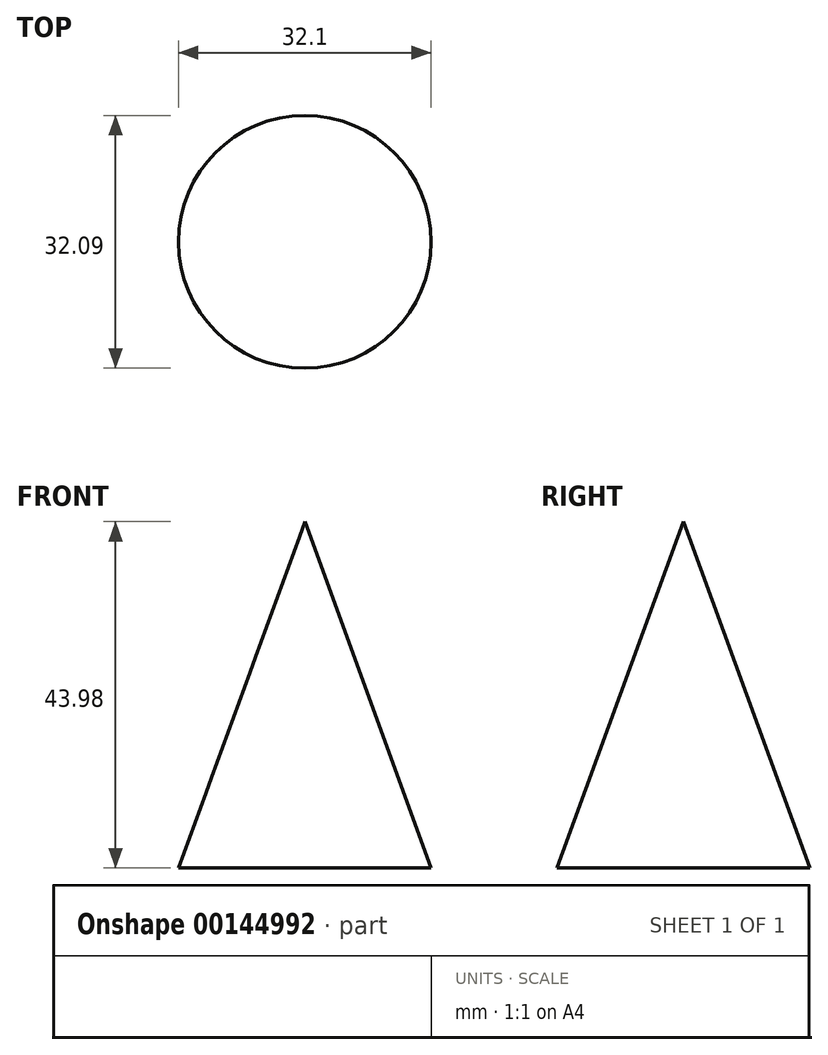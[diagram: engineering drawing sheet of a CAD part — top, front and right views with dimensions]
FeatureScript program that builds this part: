
annotation { "Feature Type Name" : "Feature", "Feature Type Description" : "" }
export const myFeature = defineFeature(function(context is Context, id is Id, definition is map)
    precondition{}
    {
        {
            var Q0;
            Q0=qCreatedBy(makeId("Right.planeOp"),FACE);
            var sketch = newSketch(context, id + "F0", { "sketchPlane" : qUnion([Q0])});
            skLineSegment(sketch, "E0", {"start": v(-14.36, -5.16) * mm, "end": v(-30.4, -49.14) * mm});
            skLineSegment(sketch, "E1", {"start": v(-30.4, -49.14) * mm, "end": v(-14.36, -49.14) * mm});
            skLineSegment(sketch, "E2", {"start": v(-14.36, -1.58) * mm, "end": v(-14.36, -57.1) * mm, "construction": true});
            skLineSegment(sketch, "E3", {"start": v(-14.36, -5.16) * mm, "end": v(-19.42, -5.16) * mm});
            skLineSegment(sketch, "E4", {"start": v(-19.42, -5.16) * mm, "end": v(-35.68, -49.72) * mm});
            skLineSegment(sketch, "E5", {"start": v(-35.68, -49.72) * mm, "end": v(-14.36, -49.72) * mm});
            skSolve(sketch);
        }
        {
            var Q0;
            Q0=sQuery(id+"F0.wireOp",EDGE,"E0");
            var Q1;
            Q1=sQuery(id+"F0.wireOp",EDGE,"E1");
            var Q2;
            Q2=sQuery(id+"F0.wireOp",EDGE,"E2");
            revolve(context, id + "F1", {"bodyType" : ToolBodyType.SURFACE, "surfaceEntities" : qUnion([Q0, Q1]), "axis" : qUnion([Q2]), "revolveType" : RevolveType.FULL});
        }
    });
